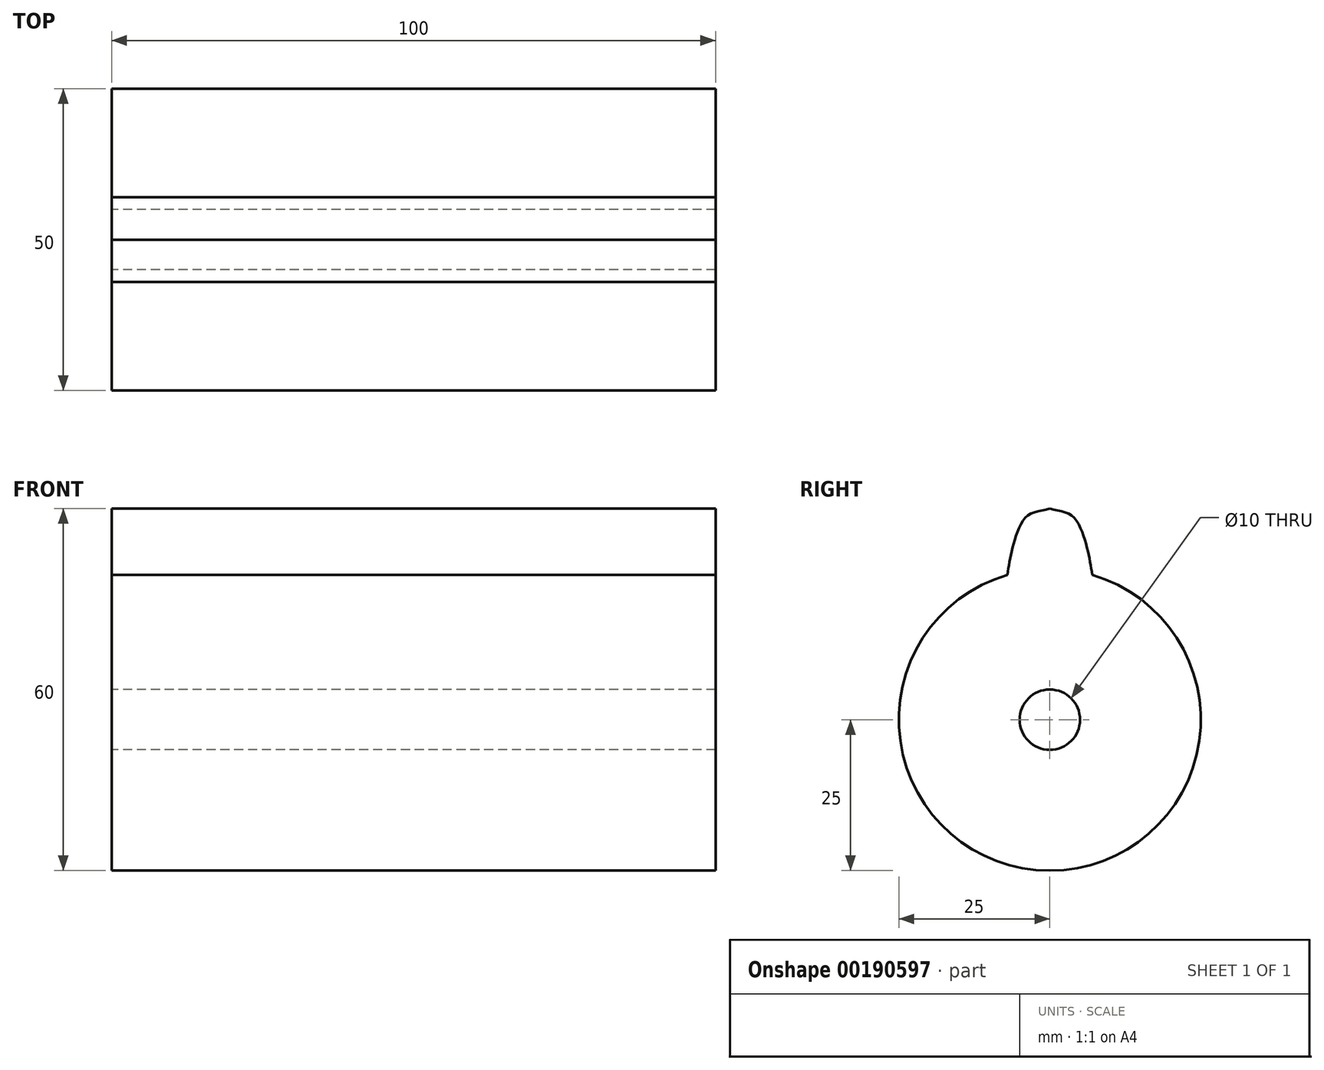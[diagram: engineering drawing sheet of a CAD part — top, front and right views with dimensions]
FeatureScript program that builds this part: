
annotation { "Feature Type Name" : "Feature", "Feature Type Description" : "" }
export const myFeature = defineFeature(function(context is Context, id is Id, definition is map)
    precondition{}
    {
        {
            var Q0;
            Q0=qCreatedBy(makeId("Right.planeOp"),FACE);
            var sketch = newSketch(context, id + "F0", { "sketchPlane" : qUnion([Q0])});
            skCircle(sketch, "E0", {"center": v(0, 0) * mm, "radius": 25 * mm});
            skFitSpline(sketch, "E1", {"points": [v(0, 35) * mm, v(3.56, 33.89) * mm, v(5.57, 30.47) * mm, v(6.56, 26.74) * mm, v(7, 24) * mm], "startDerivative": vector(14.9, -5.45) * mm, "endDerivative": vector(1.75, -12.14) * mm});
            skLineSegment(sketch, "E2", {"start": v(0, 35) * mm, "end": v(0, 25) * mm, "construction": true});
            skFitSpline(sketch, "E3.MirrorCS", {"points": [v(0, 35) * mm, v(-3.56, 33.89) * mm, v(-5.57, 30.47) * mm, v(-6.56, 26.74) * mm, v(-7, 24) * mm], "startDerivative": vector(-14.9, -5.45) * mm, "endDerivative": vector(-1.75, -12.14) * mm});
            skSolve(sketch);
        }
        {
            var Q0;
            Q0 = qSketchRegion(id + "F0", true);
            extrude(context, id + "F1", {"entities" : qUnion([Q0]), "depth" : 50 * mm, "hasSecondDirection" : true, "secondDirectionOppositeDirection" : true, "secondDirectionDepth" : 50 * mm});
        }
        {
            var Q0;
            Q0=makeQuery(id+"F1.opExtrude","CAP_FACE",FACE,{"disambiguationData":[OSD([sQuery(id+"F0.wireOp",EDGE,"E0")])],"isStart":true});
            var sketch = newSketch(context, id + "F2", { "sketchPlane" : qUnion([Q0])});
            skPoint(sketch, "E4.middle", {"position": v(0, 0) * mm});
            skCircle(sketch, "E5", {"center": v(0, 0) * mm, "radius": 5 * mm});
            skSolve(sketch);
        }
        {
            var Q0;
            Q0=makeQuery(id+"F2.imprint","IMPRINT",FACE,{"disambiguationData":[TD([[makeQuery(id+"F2.imprint","IMPRINT",EDGE,{"derivedFrom":sQuery(id+"F2.wireOp",EDGE,"E5")}),1.0]])]});
            extrude(context, id + "F3", {"entities" : qUnion([Q0]), "operationType" : NewBodyOperationType.REMOVE, "endBound" : BoundingType.UP_TO_NEXT, "oppositeDirection" : true, "depth" : 25 * mm});
        }
    });
